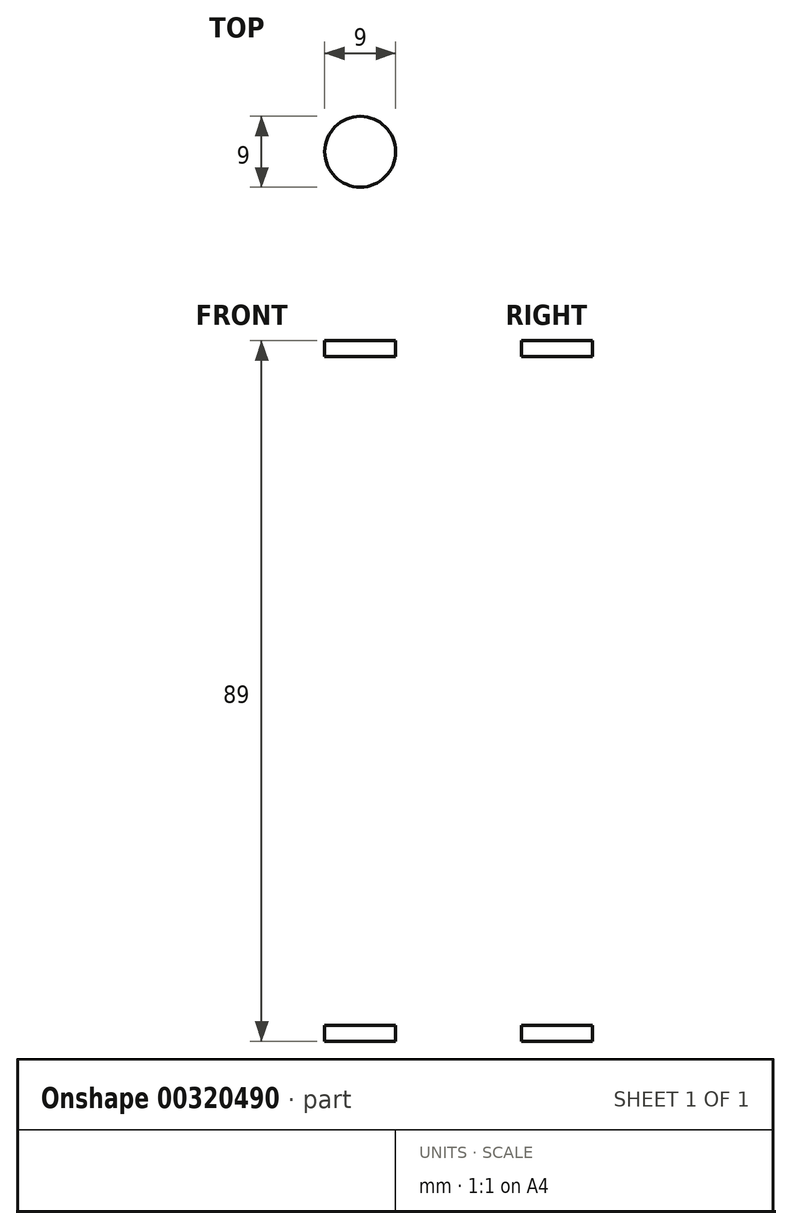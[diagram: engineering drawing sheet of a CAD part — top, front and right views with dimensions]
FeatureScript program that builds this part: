
annotation { "Feature Type Name" : "Feature", "Feature Type Description" : "" }
export const myFeature = defineFeature(function(context is Context, id is Id, definition is map)
    precondition{}
    {
        {
            var Q0;
            Q0=qCreatedBy(makeId("Front.planeOp"),FACE);
            var sketch = newSketch(context, id + "F0", { "sketchPlane" : qUnion([Q0])});
            skLineSegment(sketch, "E0.bottom", {"start": v(20, 43.26) * mm, "end": v(-20, 43.26) * mm});
            skLineSegment(sketch, "E0.top", {"start": v(20, -45.74) * mm, "end": v(-20, -45.74) * mm});
            skLineSegment(sketch, "E0.left", {"start": v(20, 43.26) * mm, "end": v(20, -45.74) * mm});
            skLineSegment(sketch, "E0.right", {"start": v(-20, 43.26) * mm, "end": v(-20, 41.26) * mm});
            skPoint(sketch, "E0.middle", {"position": v(0, -1.24) * mm});
            skLineSegment(sketch, "E1.0", {"start": v(18, 41.26) * mm, "end": v(18, -43.74) * mm});
            skLineSegment(sketch, "E1.1", {"start": v(18, 41.26) * mm, "end": v(-18, 41.26) * mm});
            skLineSegment(sketch, "E1.3", {"start": v(18, -43.74) * mm, "end": v(-18, -43.74) * mm});
            skLineSegment(sketch, "E2", {"start": v(-18, 41.26) * mm, "end": v(-20, 41.26) * mm});
            skLineSegment(sketch, "E3", {"start": v(-18, -43.74) * mm, "end": v(-20, -43.74) * mm});
            skLineSegment(sketch, "E4.trimOffspring", {"start": v(-20, -43.74) * mm, "end": v(-20, -45.74) * mm});
            skSolve(sketch);
        }
        {
            var Q0;
            Q0=makeQuery(id+"F0.imprint","IMPRINT",FACE,{"disambiguationData":[TD([[makeQuery(id+"F0.imprint","IMPRINT",EDGE,{"derivedFrom":sQuery(id+"F0.wireOp",EDGE,"E0.bottom")}),1.0]])]});
            extrude(context, id + "F1", {"entities" : qUnion([Q0]), "depth" : 130 * mm});
        }
        {
            var Q0;
            Q0=makeQuery(id+"F1.opExtrude","SWEPT_FACE",FACE,{"disambiguationData":[OSD([sQuery(id+"F0.wireOp",EDGE,"E0.bottom")])]});
            var sketch = newSketch(context, id + "F2", { "sketchPlane" : qUnion([Q0])});
            skCircle(sketch, "E5", {"center": v(0, -65) * mm, "radius": 4.5 * mm});
            skCircle(sketch, "E6.0.1.0", {"center": v(0, -20) * mm, "radius": 4.5 * mm});
            skLineSegment(sketch, "E6.direction1", {"start": v(0, -65) * mm, "end": v(25, -65) * mm, "construction": true});
            skLineSegment(sketch, "E6.direction2", {"start": v(0, -65) * mm, "end": v(0, -20) * mm, "construction": true});
            skCircle(sketch, "E7.MirrorC", {"center": v(0, -110) * mm, "radius": 4.5 * mm});
            skSolve(sketch);
        }
        {
            var Q0;
            Q0=makeQuery(id+"F2.imprint","IMPRINT",FACE,{"disambiguationData":[TD([[makeQuery(id+"F2.imprint","IMPRINT",EDGE,{"derivedFrom":sQuery(id+"F2.wireOp",EDGE,"E6.0.1.0")}),1.0]])]});
            var Q1;
            Q1=makeQuery(id+"F2.imprint","IMPRINT",FACE,{"disambiguationData":[TD([[makeQuery(id+"F2.imprint","IMPRINT",EDGE,{"derivedFrom":sQuery(id+"F2.wireOp",EDGE,"E5")}),1.0]])]});
            var Q2;
            Q2=makeQuery(id+"F2.imprint","IMPRINT",FACE,{"disambiguationData":[TD([[makeQuery(id+"F2.imprint","IMPRINT",EDGE,{"derivedFrom":sQuery(id+"F2.wireOp",EDGE,"E7.MirrorC")}),-1.0]])]});
            extrude(context, id + "F3", {"entities" : qUnion([Q0, Q1, Q2]), "operationType" : NewBodyOperationType.REMOVE, "oppositeDirection" : true, "depth" : 130 * mm});
        }
    });
